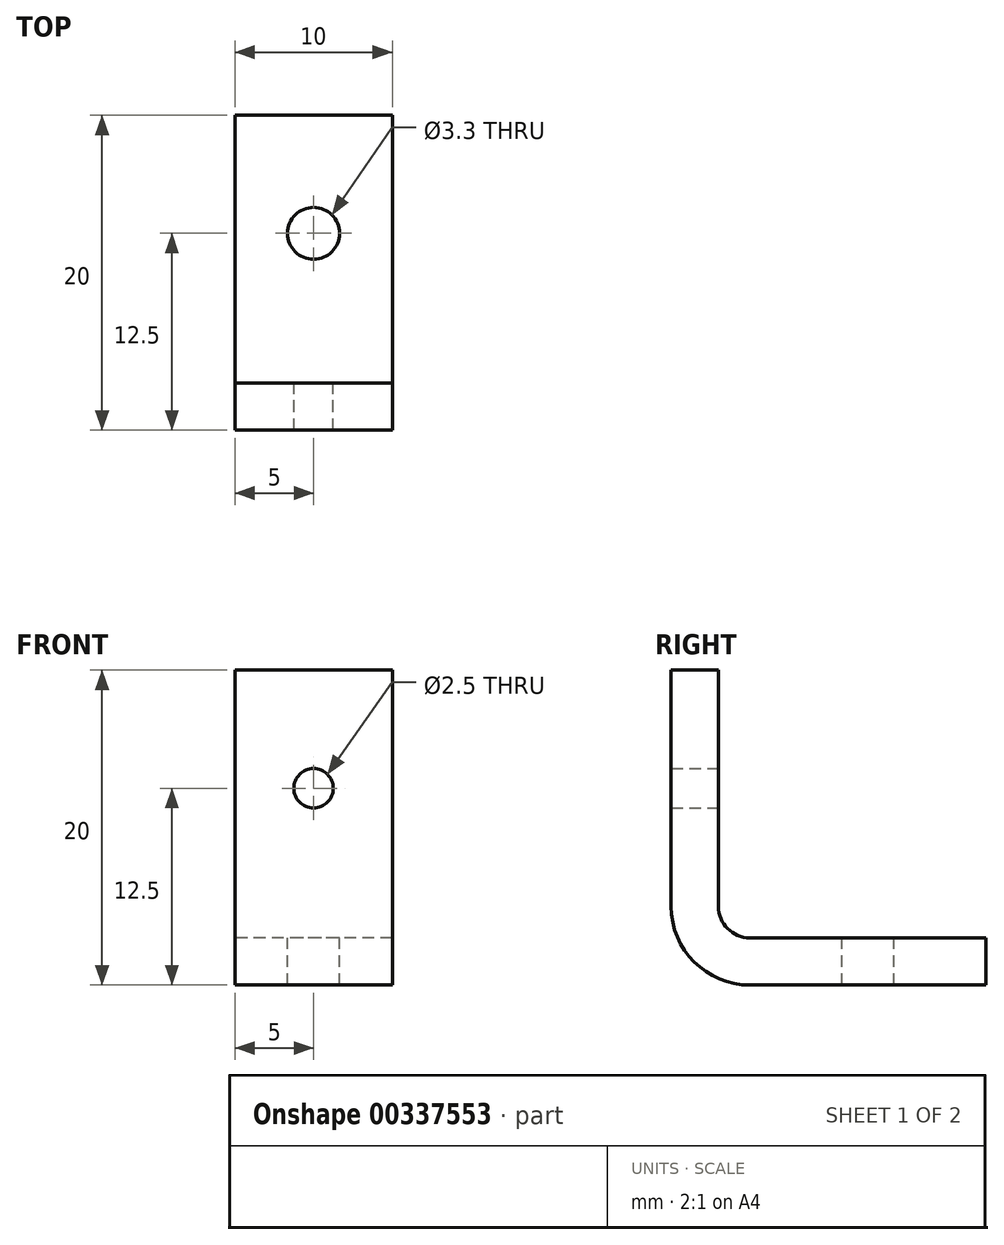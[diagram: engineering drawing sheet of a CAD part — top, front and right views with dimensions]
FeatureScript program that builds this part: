
annotation { "Feature Type Name" : "Feature", "Feature Type Description" : "" }
export const myFeature = defineFeature(function(context is Context, id is Id, definition is map)
    precondition{}
    {
        {
            var Q0;
            Q0=qCreatedBy(makeId("Right.planeOp"),FACE);
            var sketch = newSketch(context, id + "F0", { "sketchPlane" : qUnion([Q0])});
            skLineSegment(sketch, "E0", {"start": v(20, 0) * mm, "end": v(5, 0) * mm});
            skLineSegment(sketch, "E1", {"start": v(0, 5) * mm, "end": v(0, 20) * mm});
            skPoint(sketch, "E2.visualSharp", {"position": v(0, 0) * mm});
            skArc(sketch, "E2.filletArc", {"start": v(0, 5) * mm, "mid": v(1.46, 1.46) * mm, "end": v(5, 0) * mm});
            skSolve(sketch);
        }
        {
            var Q0;
            Q0=sQuery(id+"F0.wireOp",EDGE,"E0");
            var Q1;
            Q1=sQuery(id+"F0.wireOp",VERTEX,"E0.start");
            cPlane(context, id + "F1", {"entities" : qUnion([Q0, Q1]), "cplaneType" : CPlaneType.LINE_POINT, "offset" : 25 * mm, "width" : 150 * mm, "height" : 150 * mm});
        }
        {
            var Q0;
            Q0=qCreatedBy(id+"F1.planeOp",FACE);
            var sketch = newSketch(context, id + "F2", { "sketchPlane" : qUnion([Q0])});
            skLineSegment(sketch, "E3.bottom", {"start": v(0, 0) * mm, "end": v(-10, 0) * mm});
            skLineSegment(sketch, "E3.top", {"start": v(0, 3) * mm, "end": v(-10, 3) * mm});
            skLineSegment(sketch, "E3.left", {"start": v(0, 0) * mm, "end": v(0, 3) * mm});
            skLineSegment(sketch, "E3.right", {"start": v(-10, 0) * mm, "end": v(-10, 3) * mm});
            skSolve(sketch);
        }
        {
            var Q0;
            Q0 = qSketchRegion(id + "F2", true);
            var Q1;
            Q1 = qConstructionFilter(qBodyType(qCreatedBy(id + "F0" ,EDGE), BodyType.WIRE), ConstructionObject.NO);
            sweep(context, id + "F3", {"profiles" : qUnion([Q0]), "path" : qUnion([Q1])});
        }
        {
            var Q0;
            Q0=makeQuery(id+"F3.opSweep","SWEPT_FACE",FACE,{"disambiguationData":[OSD([sQuery(id+"F0.wireOp",EDGE,"E0"),sQuery(id+"F2.wireOp",EDGE,"E3.top")])]});
            var sketch = newSketch(context, id + "F4", { "sketchPlane" : qUnion([Q0])});
            skCircle(sketch, "E4", {"center": v(-5, 12.5) * mm, "radius": 1.96 * mm, "construction": true});
            skPoint(sketch, "E4.centerSnap0", {"position": v(-5, 20) * mm});
            skPoint(sketch, "E4.centerSnap1", {"position": v(0, 12.5) * mm});
            skSolve(sketch);
        }
        {
            var Q0;
            Q0=sQuery(id+"F4.wireOp",VERTEX,"E4.center");
            var Q1;
            Q1=makeQuery(id+"F3.opSweep","SWEPT_BODY",BODY,{"disambiguationData":[OSD([sQuery(id+"F0.wireOp",EDGE,"E0"),sQuery(id+"F2.wireOp",EDGE,"E3.bottom"),sQuery(id+"F2.wireOp",EDGE,"E3.top"),sQuery(id+"F2.wireOp",EDGE,"E3.left"),sQuery(id+"F2.wireOp",EDGE,"E3.right")])]});
            hole(context, id + "F5", {"style" : HoleStyle.SIMPLE, "endStyle" : HoleEndStyle.THROUGH, "standardTappedOrClearance" : lookupTablePath({ "standard" : "ISO", "fit" : "Normal", "size" : "M3", "type" : "Clearance" }), "standardBlindInLast" : lookupTablePath({ "fit" : "Standard", "standard" : "ISO", "size" : "M3", "type" : "Clearance" }), "holeDiameter" : 3.3 * mm, "isTappedThrough" : true, "tappedDepth" : 12 * mm, "tapClearance" : 3, "locations" : qUnion([Q0]), "scope" : qUnion([Q1])});
        }
        {
            var Q0;
            Q0=makeQuery(id+"F3.opSweep","SWEPT_FACE",FACE,{"disambiguationData":[OSD([sQuery(id+"F0.wireOp",EDGE,"E1"),sQuery(id+"F2.wireOp",EDGE,"E3.top")])]});
            var sketch = newSketch(context, id + "F6", { "sketchPlane" : qUnion([Q0])});
            skCircle(sketch, "E5", {"center": v(5, 12.5) * mm, "radius": 1.78 * mm, "construction": true});
            skPoint(sketch, "E5.centerSnap0", {"position": v(5, 20) * mm});
            skPoint(sketch, "E5.centerSnap1", {"position": v(10, 12.5) * mm});
            skSolve(sketch);
        }
        {
            var Q0;
            Q0=sQuery(id+"F6.wireOp",VERTEX,"E5.center");
            var Q1;
            Q1=makeQuery(id+"F3.opSweep","SWEPT_BODY",BODY,{"disambiguationData":[OSD([sQuery(id+"F0.wireOp",EDGE,"E0"),sQuery(id+"F2.wireOp",EDGE,"E3.bottom"),sQuery(id+"F2.wireOp",EDGE,"E3.top"),sQuery(id+"F2.wireOp",EDGE,"E3.left"),sQuery(id+"F2.wireOp",EDGE,"E3.right")])]});
            hole(context, id + "F7", {"style" : HoleStyle.SIMPLE, "endStyle" : HoleEndStyle.THROUGH, "standardTappedOrClearance" : lookupTablePath({ "standard" : "ISO", "engagement" : "75%", "pitch" : "0.5 mm", "size" : "M3", "type" : "Tapped" }), "standardBlindInLast" : lookupTablePath({ "standard" : "ISO", "engagement" : "75%", "pitch" : "0.5 mm", "size" : "M3", "type" : "Tapped" }), "holeDiameter" : 2.5 * mm, "showTappedDepth" : true, "isTappedThrough" : true, "tappedDepth" : 12 * mm, "tapClearance" : 3, "locations" : qUnion([Q0]), "scope" : qUnion([Q1]), "majorDiameter" : 3 * mm});
        }
    });
